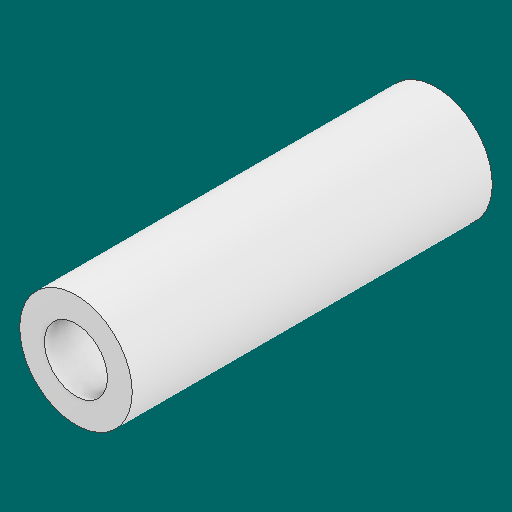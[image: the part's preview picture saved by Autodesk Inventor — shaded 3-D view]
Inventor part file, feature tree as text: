
AUTODESK INVENTOR PART (.ipt)
format: ipt  version: 2023.1 (Build 271208000, 208)  size: 96,768 bytes
history: native  units: in
note: dims shown in document units (in); Inventor stores cm internally (conversion verified against a paired STEP export)
features: other x3, sketch x1
ambient origin geometry x8: Origin, YZ Plane, XZ Plane, XY Plane, X Axis, Y Axis, Z Axis, Center Point
bodies: Solid1 (feature_tree)
feature tree (4):
  other  "1.2inSpacer.ipt"
  other  "Solid1::1.2inSpacer.ipt"
  other  "TaggingFeature1"
  sketch  "Sketch1"  dims[d0=0.3937in]
